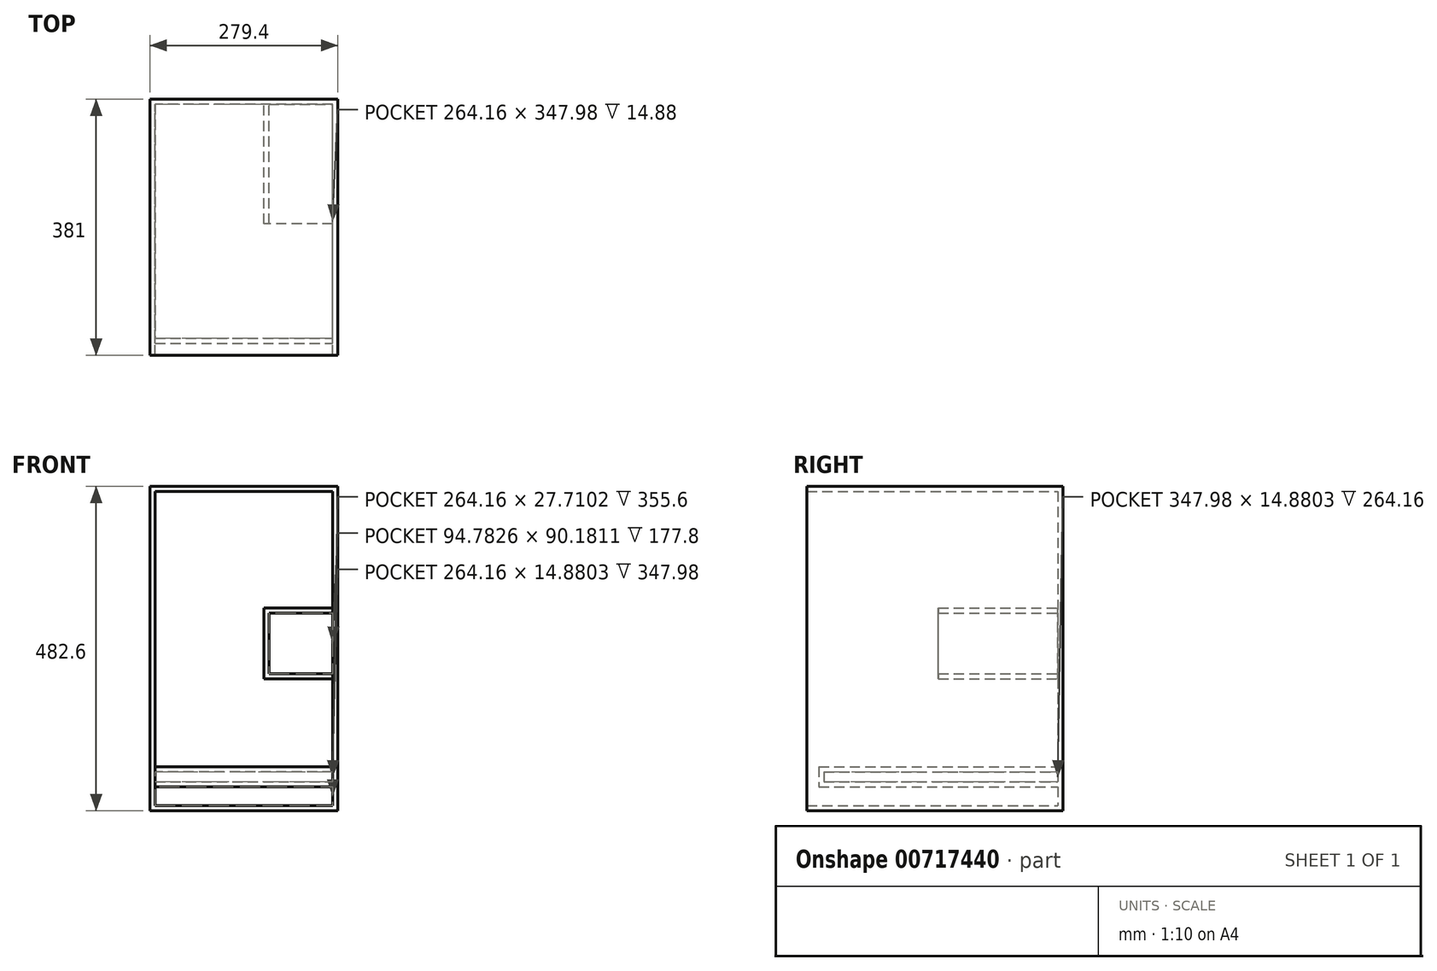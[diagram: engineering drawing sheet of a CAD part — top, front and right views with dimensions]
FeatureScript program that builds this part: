
annotation { "Feature Type Name" : "Feature", "Feature Type Description" : "" }
export const myFeature = defineFeature(function(context is Context, id is Id, definition is map)
    precondition{}
    {
        {
            var Q0;
            Q0=qCreatedBy(makeId("Front.planeOp"),FACE);
            var sketch = newSketch(context, id + "F0", { "sketchPlane" : qUnion([Q0])});
            skLineSegment(sketch, "E0.bottom", {"start": v(139.7, 241.3) * mm, "end": v(-139.7, 241.3) * mm});
            skLineSegment(sketch, "E0.top", {"start": v(139.7, -241.3) * mm, "end": v(-139.7, -241.3) * mm});
            skLineSegment(sketch, "E0.left", {"start": v(139.7, 241.3) * mm, "end": v(139.7, -241.3) * mm});
            skLineSegment(sketch, "E0.right", {"start": v(-139.7, 241.3) * mm, "end": v(-139.7, -241.3) * mm});
            skPoint(sketch, "E0.middle", {"position": v(0, 0) * mm});
            skSolve(sketch);
        }
        {
            var Q0;
            Q0=makeQuery(id+"F0.imprint","IMPRINT",FACE,{"disambiguationData":[TD([[makeQuery(id+"F0.imprint","IMPRINT",EDGE,{"derivedFrom":sQuery(id+"F0.wireOp",EDGE,"E0.bottom")}),1.0]])]});
            extrude(context, id + "F1", {"entities" : qUnion([Q0]), "depth" : 381 * mm, "offsetDistance" : 25.4 * mm});
        }
        {
            var Q0;
            Q0=makeQuery(id+"F1.opExtrude","CAP_FACE",FACE,{"disambiguationData":[OSD([sQuery(id+"F0.wireOp",EDGE,"E0.bottom"),sQuery(id+"F0.wireOp",EDGE,"E0.top"),sQuery(id+"F0.wireOp",EDGE,"E0.left"),sQuery(id+"F0.wireOp",EDGE,"E0.right")])],"isStart":false});
            shell(context, id + "F2", {"entities" : qUnion([Q0]), "thickness" : 7.62 * mm});
        }
        {
            var Q0;
            Q0=makeQuery(id+"F2.opShell","OFFSET_FACE",FACE,{"disambiguationData":[OSD([sQuery(id+"F0.wireOp",EDGE,"E0.bottom"),sQuery(id+"F0.wireOp",EDGE,"E0.top"),sQuery(id+"F0.wireOp",EDGE,"E0.left"),sQuery(id+"F0.wireOp",EDGE,"E0.right")])]});
            var sketch = newSketch(context, id + "F3", { "sketchPlane" : qUnion([Q0])});
            skLineSegment(sketch, "E1.bottom", {"start": v(-132.08, -175.85) * mm, "end": v(132.08, -175.85) * mm});
            skLineSegment(sketch, "E1.top", {"start": v(-132.08, -205.97) * mm, "end": v(132.08, -205.97) * mm});
            skLineSegment(sketch, "E1.left", {"start": v(-132.08, -175.85) * mm, "end": v(-132.08, -205.97) * mm});
            skLineSegment(sketch, "E1.right", {"start": v(132.08, -175.85) * mm, "end": v(132.08, -205.97) * mm});
            skSolve(sketch);
        }
        {
            var Q0;
            Q0 = qSketchRegion(id + "F3", true);
            extrude(context, id + "F4", {"entities" : qUnion([Q0]), "operationType" : NewBodyOperationType.ADD, "depth" : 355.6 * mm, "offsetDistance" : 25.4 * mm});
        }
        {
            var Q0;
            {var subQ0=sQuery(id+"F0.wireOp",EDGE,"E0.bottom");var subQ1=sQuery(id+"F0.wireOp",EDGE,"E0.left");var subQ2=sQuery(id+"F0.wireOp",EDGE,"E0.right");Q0=makeQuery(id+"F4.boolean.opBoolean","SPLIT",FACE,{"disambiguationData":[TD([makeQuery(id+"F2.opShell","OFFSET_FACE",FACE,{"disambiguationData":[OSD([subQ0])]})])],"derivedFrom":makeQuery(id+"F2.opShell","OFFSET_FACE",FACE,{"disambiguationData":[OSD([subQ0,sQuery(id+"F0.wireOp",EDGE,"E0.top"),subQ1,subQ2])]})});}
            var sketch = newSketch(context, id + "F5", { "sketchPlane" : qUnion([Q0])});
            skLineSegment(sketch, "E2.bottom", {"start": v(132.08, -44.74) * mm, "end": v(29.68, -44.74) * mm});
            skLineSegment(sketch, "E2.top", {"start": v(132.08, 60.68) * mm, "end": v(29.68, 60.68) * mm});
            skLineSegment(sketch, "E2.left", {"start": v(132.08, -44.74) * mm, "end": v(132.08, 60.68) * mm});
            skLineSegment(sketch, "E2.right", {"start": v(29.68, -44.74) * mm, "end": v(29.68, 60.68) * mm});
            skSolve(sketch);
        }
        {
            var Q0;
            Q0 = qSketchRegion(id + "F5", true);
            extrude(context, id + "F6", {"entities" : qUnion([Q0]), "operationType" : NewBodyOperationType.ADD, "depth" : 177.8 * mm, "offsetDistance" : 25.4 * mm});
        }
        {
            var Q0;
            Q0=makeQuery(id+"F6.opExtrude","CAP_FACE",FACE,{"disambiguationData":[OSD([sQuery(id+"F5.wireOp",EDGE,"E2.bottom"),sQuery(id+"F5.wireOp",EDGE,"E2.top"),sQuery(id+"F5.wireOp",EDGE,"E2.left"),sQuery(id+"F5.wireOp",EDGE,"E2.right")])],"isStart":false});
            extrude(context, id + "F7", {"entities" : qUnion([Q0]), "operationType" : NewBodyOperationType.ADD, "oppositeDirection" : true, "depth" : 177.8 * mm, "offsetDistance" : 25.4 * mm});
        }
        {
            var Q0;
            Q0=makeQuery(id+"F6.opExtrude","CAP_FACE",FACE,{"disambiguationData":[OSD([sQuery(id+"F5.wireOp",EDGE,"E2.bottom"),sQuery(id+"F5.wireOp",EDGE,"E2.top"),sQuery(id+"F5.wireOp",EDGE,"E2.left"),sQuery(id+"F5.wireOp",EDGE,"E2.right")])],"isStart":false});
            shell(context, id + "F8", {"entities" : qUnion([Q0]), "thickness" : 7.62 * mm});
        }
    });
